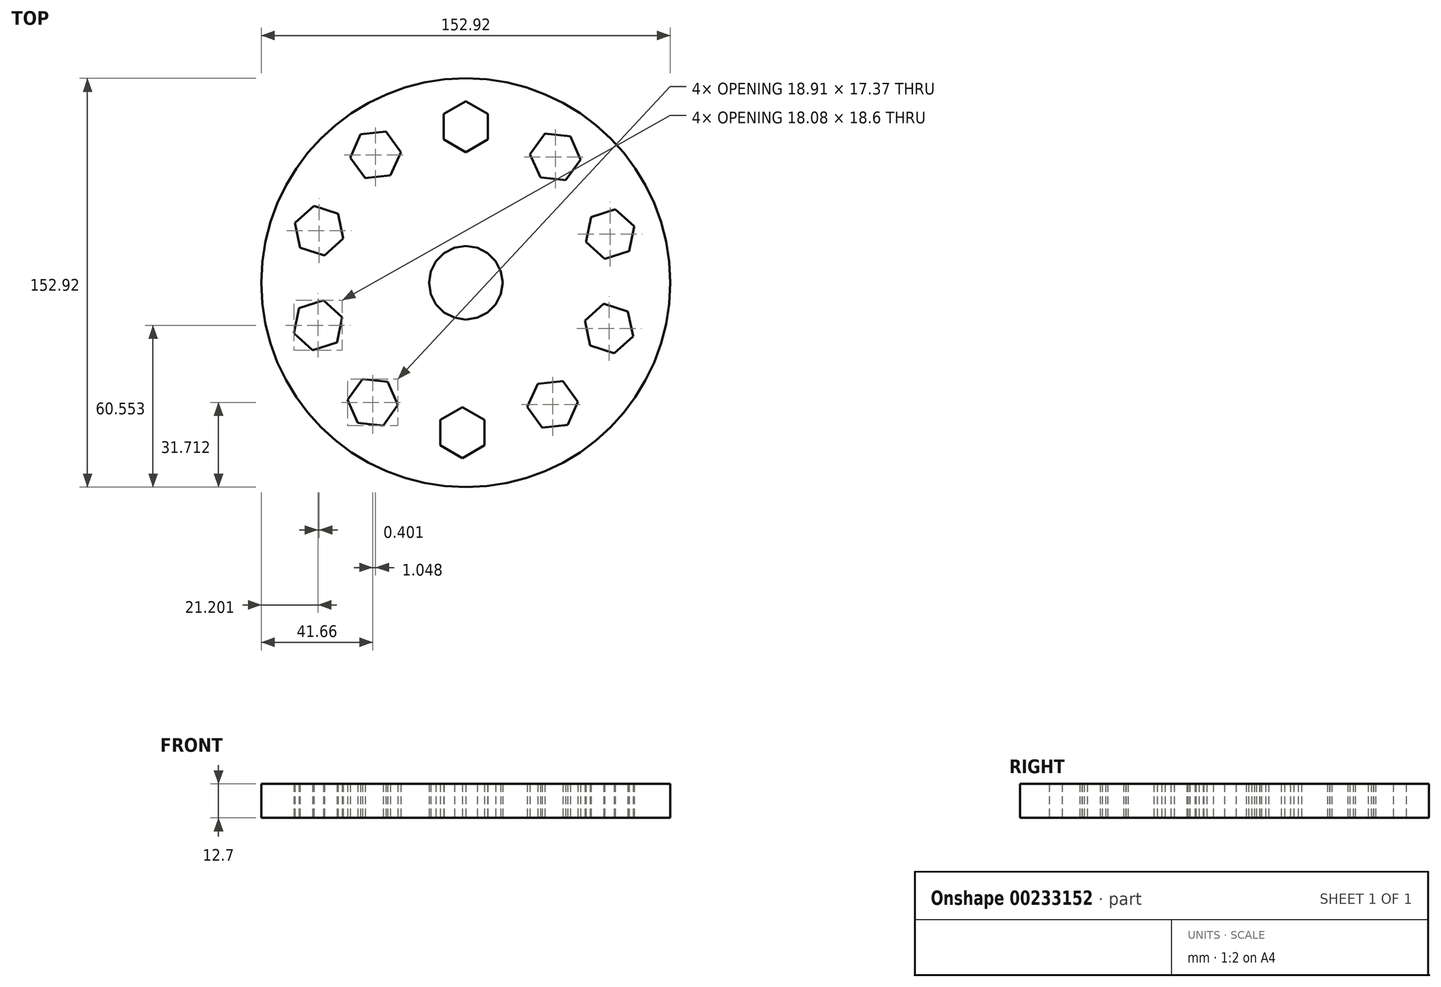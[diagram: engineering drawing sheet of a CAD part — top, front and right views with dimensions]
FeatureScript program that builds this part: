
annotation { "Feature Type Name" : "Feature", "Feature Type Description" : "" }
export const myFeature = defineFeature(function(context is Context, id is Id, definition is map)
    precondition{}
    {
        {
            var Q0;
            Q0=qCreatedBy(makeId("Top.planeOp"),FACE);
            var sketch = newSketch(context, id + "F0", { "sketchPlane" : qUnion([Q0])});
            skCircle(sketch, "E0", {"center": v(0, 0) * mm, "radius": 76.46 * mm});
            skCircle(sketch, "E1", {"center": v(0, 0) * mm, "radius": 67.87 * mm});
            skCircle(sketch, "E2.cCircle", {"center": v(0, 58.37) * mm, "radius": 8.23 * mm, "construction": true});
            skLineSegment(sketch, "E2.0", {"start": v(8.23, 53.61) * mm, "end": v(0, 48.86) * mm});
            skLineSegment(sketch, "E2.1", {"start": v(0, 48.86) * mm, "end": v(-8.23, 53.61) * mm});
            skLineSegment(sketch, "E2.2", {"start": v(-8.23, 53.61) * mm, "end": v(-8.23, 63.12) * mm});
            skLineSegment(sketch, "E2.3", {"start": v(-8.23, 63.12) * mm, "end": v(0, 67.87) * mm});
            skLineSegment(sketch, "E2.4", {"start": v(0, 67.87) * mm, "end": v(8.23, 63.12) * mm});
            skLineSegment(sketch, "E2.5", {"start": v(8.23, 63.12) * mm, "end": v(8.23, 53.61) * mm});
            skPoint(sketch, "E2.0.midPoint", {"position": v(4.12, 51.24) * mm});
            skLineSegment(sketch, "E3.1.0", {"start": v(-39.34, 55.51) * mm, "end": v(-29.89, 56.5) * mm});
            skLineSegment(sketch, "E3.1.1", {"start": v(-29.89, 56.5) * mm, "end": v(-24.3, 48.82) * mm});
            skLineSegment(sketch, "E3.1.2", {"start": v(-24.3, 48.82) * mm, "end": v(-28.16, 40.13) * mm});
            skLineSegment(sketch, "E3.1.3", {"start": v(-28.16, 40.13) * mm, "end": v(-37.62, 39.14) * mm});
            skLineSegment(sketch, "E3.1.4", {"start": v(-37.62, 39.14) * mm, "end": v(-43.2, 46.83) * mm});
            skLineSegment(sketch, "E3.1.5", {"start": v(-43.2, 46.83) * mm, "end": v(-39.34, 55.51) * mm});
            skLineSegment(sketch, "E3.2.0", {"start": v(-63.9, 22.39) * mm, "end": v(-56.84, 28.75) * mm});
            skLineSegment(sketch, "E3.2.1", {"start": v(-56.84, 28.75) * mm, "end": v(-47.8, 25.81) * mm});
            skLineSegment(sketch, "E3.2.2", {"start": v(-47.8, 25.81) * mm, "end": v(-45.82, 16.51) * mm});
            skLineSegment(sketch, "E3.2.3", {"start": v(-45.82, 16.51) * mm, "end": v(-52.88, 10.15) * mm});
            skLineSegment(sketch, "E3.2.4", {"start": v(-52.88, 10.15) * mm, "end": v(-61.92, 13.1) * mm});
            skLineSegment(sketch, "E3.2.5", {"start": v(-61.92, 13.1) * mm, "end": v(-63.9, 22.39) * mm});
            skLineSegment(sketch, "E3.3.0", {"start": v(-64.3, -18.84) * mm, "end": v(-62.32, -9.55) * mm});
            skLineSegment(sketch, "E3.3.1", {"start": v(-62.32, -9.55) * mm, "end": v(-53.28, -6.6) * mm});
            skLineSegment(sketch, "E3.3.2", {"start": v(-53.28, -6.6) * mm, "end": v(-46.22, -12.97) * mm});
            skLineSegment(sketch, "E3.3.3", {"start": v(-46.22, -12.97) * mm, "end": v(-48.2, -22.27) * mm});
            skLineSegment(sketch, "E3.3.4", {"start": v(-48.2, -22.27) * mm, "end": v(-57.24, -25.2) * mm});
            skLineSegment(sketch, "E3.3.5", {"start": v(-57.24, -25.2) * mm, "end": v(-64.3, -18.84) * mm});
            skLineSegment(sketch, "E3.4.0", {"start": v(-40.39, -52.44) * mm, "end": v(-44.25, -43.75) * mm});
            skLineSegment(sketch, "E3.4.1", {"start": v(-44.25, -43.75) * mm, "end": v(-38.67, -36.06) * mm});
            skLineSegment(sketch, "E3.4.2", {"start": v(-38.67, -36.06) * mm, "end": v(-29.21, -37.06) * mm});
            skLineSegment(sketch, "E3.4.3", {"start": v(-29.21, -37.06) * mm, "end": v(-25.35, -45.74) * mm});
            skLineSegment(sketch, "E3.4.4", {"start": v(-25.35, -45.74) * mm, "end": v(-30.93, -53.43) * mm});
            skLineSegment(sketch, "E3.4.5", {"start": v(-30.93, -53.43) * mm, "end": v(-40.39, -52.44) * mm});
            skLineSegment(sketch, "E3.5.0", {"start": v(-1.3, -65.56) * mm, "end": v(-9.53, -60.8) * mm});
            skLineSegment(sketch, "E3.5.1", {"start": v(-9.53, -60.8) * mm, "end": v(-9.53, -51.3) * mm});
            skLineSegment(sketch, "E3.5.2", {"start": v(-9.53, -51.3) * mm, "end": v(-1.3, -46.55) * mm});
            skLineSegment(sketch, "E3.5.3", {"start": v(-1.3, -46.55) * mm, "end": v(6.94, -51.3) * mm});
            skLineSegment(sketch, "E3.5.4", {"start": v(6.94, -51.3) * mm, "end": v(6.94, -60.8) * mm});
            skLineSegment(sketch, "E3.5.5", {"start": v(6.94, -60.8) * mm, "end": v(-1.3, -65.56) * mm});
            skLineSegment(sketch, "E3.6.0", {"start": v(38.04, -53.2) * mm, "end": v(28.59, -54.2) * mm});
            skLineSegment(sketch, "E3.6.1", {"start": v(28.59, -54.2) * mm, "end": v(23, -46.5) * mm});
            skLineSegment(sketch, "E3.6.2", {"start": v(23, -46.5) * mm, "end": v(26.87, -37.82) * mm});
            skLineSegment(sketch, "E3.6.3", {"start": v(26.87, -37.82) * mm, "end": v(36.32, -36.83) * mm});
            skLineSegment(sketch, "E3.6.4", {"start": v(36.32, -36.83) * mm, "end": v(41.91, -44.52) * mm});
            skLineSegment(sketch, "E3.6.5", {"start": v(41.91, -44.52) * mm, "end": v(38.04, -53.2) * mm});
            skLineSegment(sketch, "E3.7.0", {"start": v(62.6, -20.08) * mm, "end": v(55.54, -26.44) * mm});
            skLineSegment(sketch, "E3.7.1", {"start": v(55.54, -26.44) * mm, "end": v(46.5, -23.5) * mm});
            skLineSegment(sketch, "E3.7.2", {"start": v(46.5, -23.5) * mm, "end": v(44.52, -14.2) * mm});
            skLineSegment(sketch, "E3.7.3", {"start": v(44.52, -14.2) * mm, "end": v(51.59, -7.84) * mm});
            skLineSegment(sketch, "E3.7.4", {"start": v(51.59, -7.84) * mm, "end": v(60.63, -10.78) * mm});
            skLineSegment(sketch, "E3.7.5", {"start": v(60.63, -10.78) * mm, "end": v(62.6, -20.08) * mm});
            skLineSegment(sketch, "E3.8.0", {"start": v(63, 21.16) * mm, "end": v(61.03, 11.86) * mm});
            skLineSegment(sketch, "E3.8.1", {"start": v(61.03, 11.86) * mm, "end": v(51.99, 8.92) * mm});
            skLineSegment(sketch, "E3.8.2", {"start": v(51.99, 8.92) * mm, "end": v(44.92, 15.28) * mm});
            skLineSegment(sketch, "E3.8.3", {"start": v(44.92, 15.28) * mm, "end": v(46.9, 24.58) * mm});
            skLineSegment(sketch, "E3.8.4", {"start": v(46.9, 24.58) * mm, "end": v(55.94, 27.52) * mm});
            skLineSegment(sketch, "E3.8.5", {"start": v(55.94, 27.52) * mm, "end": v(63, 21.16) * mm});
            skLineSegment(sketch, "E3.9.0", {"start": v(39.1, 54.75) * mm, "end": v(42.96, 46.07) * mm});
            skLineSegment(sketch, "E3.9.1", {"start": v(42.96, 46.07) * mm, "end": v(37.37, 38.38) * mm});
            skLineSegment(sketch, "E3.9.2", {"start": v(37.37, 38.38) * mm, "end": v(27.92, 39.37) * mm});
            skLineSegment(sketch, "E3.9.3", {"start": v(27.92, 39.37) * mm, "end": v(24.05, 48.05) * mm});
            skLineSegment(sketch, "E3.9.4", {"start": v(24.05, 48.05) * mm, "end": v(29.64, 55.74) * mm});
            skLineSegment(sketch, "E3.9.5", {"start": v(29.64, 55.74) * mm, "end": v(39.1, 54.75) * mm});
            skCircle(sketch, "E4.cCircle", {"center": v(0, 0) * mm, "radius": 13.6 * mm, "construction": true});
            skLineSegment(sketch, "E4.0", {"start": v(8.1, 11.14) * mm, "end": v(4.26, 13.1) * mm});
            skLineSegment(sketch, "E4.1", {"start": v(11.14, 8.1) * mm, "end": v(8.1, 11.14) * mm});
            skLineSegment(sketch, "E4.2", {"start": v(13.1, 4.26) * mm, "end": v(11.14, 8.1) * mm});
            skLineSegment(sketch, "E4.3", {"start": v(13.77, 0) * mm, "end": v(13.1, 4.26) * mm});
            skLineSegment(sketch, "E4.4", {"start": v(13.1, -4.26) * mm, "end": v(13.77, 0) * mm});
            skLineSegment(sketch, "E4.5", {"start": v(11.14, -8.1) * mm, "end": v(13.1, -4.26) * mm});
            skLineSegment(sketch, "E4.6", {"start": v(8.1, -11.14) * mm, "end": v(11.14, -8.1) * mm});
            skLineSegment(sketch, "E4.7", {"start": v(4.26, -13.1) * mm, "end": v(8.1, -11.14) * mm});
            skLineSegment(sketch, "E4.8", {"start": v(0, -13.77) * mm, "end": v(4.26, -13.1) * mm});
            skLineSegment(sketch, "E4.9", {"start": v(-4.26, -13.1) * mm, "end": v(0, -13.77) * mm});
            skLineSegment(sketch, "E4.10", {"start": v(-8.1, -11.14) * mm, "end": v(-4.26, -13.1) * mm});
            skLineSegment(sketch, "E4.11", {"start": v(-11.14, -8.1) * mm, "end": v(-8.1, -11.14) * mm});
            skLineSegment(sketch, "E4.12", {"start": v(-13.1, -4.26) * mm, "end": v(-11.14, -8.1) * mm});
            skLineSegment(sketch, "E4.13", {"start": v(-13.77, 0) * mm, "end": v(-13.1, -4.26) * mm});
            skLineSegment(sketch, "E4.14", {"start": v(-13.1, 4.26) * mm, "end": v(-13.77, 0) * mm});
            skLineSegment(sketch, "E4.15", {"start": v(-11.14, 8.1) * mm, "end": v(-13.1, 4.26) * mm});
            skLineSegment(sketch, "E4.16", {"start": v(-8.1, 11.14) * mm, "end": v(-11.14, 8.1) * mm});
            skLineSegment(sketch, "E4.17", {"start": v(-4.26, 13.1) * mm, "end": v(-8.1, 11.14) * mm});
            skLineSegment(sketch, "E4.18", {"start": v(0, 13.77) * mm, "end": v(-4.26, 13.1) * mm});
            skLineSegment(sketch, "E4.19", {"start": v(4.26, 13.1) * mm, "end": v(0, 13.77) * mm});
            skPoint(sketch, "E4.0.midPoint", {"position": v(6.18, 12.12) * mm});
            skSolve(sketch);
        }
        {
            var Q0;
            Q0=makeQuery(id+"F0.imprint","IMPRINT",FACE,{"disambiguationData":[TD([[makeQuery(id+"F0.imprint","IMPRINT",EDGE,{"derivedFrom":sQuery(id+"F0.wireOp",EDGE,"E2.0")}),1.0]])]});
            var Q1;
            Q1=makeQuery(id+"F0.imprint","IMPRINT",FACE,{"disambiguationData":[TD([[makeQuery(id+"F0.imprint","IMPRINT",EDGE,{"derivedFrom":sQuery(id+"F0.wireOp",EDGE,"E0")}),1.0]])]});
            extrude(context, id + "F1", {"entities" : qUnion([Q0, Q1]), "depth" : 12.7 * mm});
        }
    });
